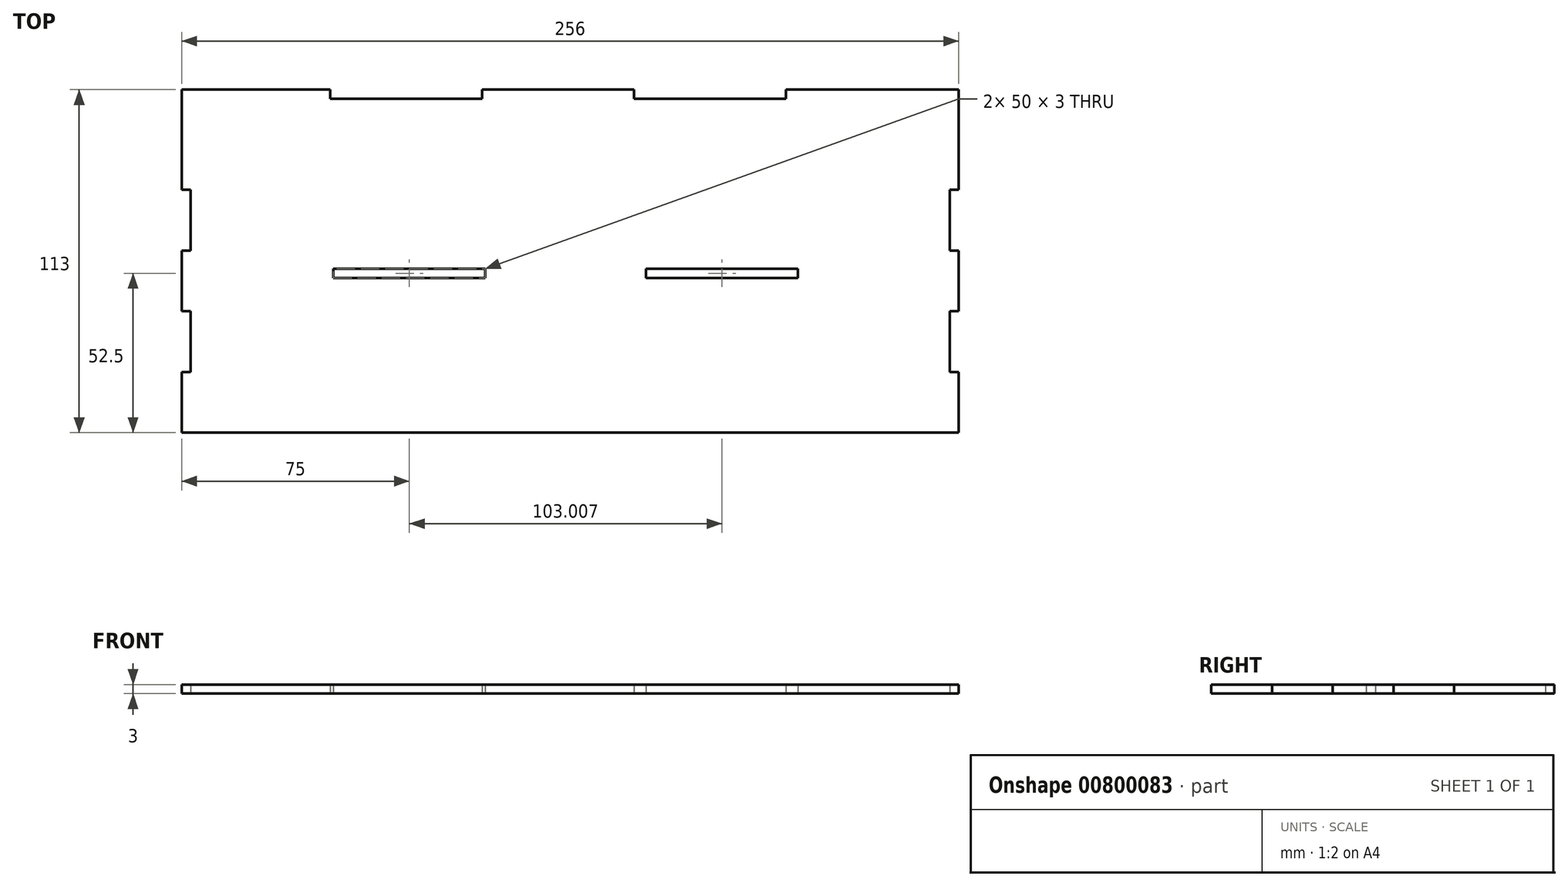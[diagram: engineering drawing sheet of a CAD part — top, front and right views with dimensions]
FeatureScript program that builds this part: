
annotation { "Feature Type Name" : "Feature", "Feature Type Description" : "" }
export const myFeature = defineFeature(function(context is Context, id is Id, definition is map)
    precondition{}
    {
        {
            var Q0;
            Q0=qCreatedBy(makeId("Top.planeOp"),FACE);
            var sketch = newSketch(context, id + "F0", { "sketchPlane" : qUnion([Q0])});
            skLineSegment(sketch, "E0.bottom", {"start": v(-250, 0) * mm, "end": v(0, 0) * mm});
            skLineSegment(sketch, "E0.top", {"start": v(-250, -110) * mm, "end": v(0, -110) * mm});
            skLineSegment(sketch, "E0.left", {"start": v(-250, 0) * mm, "end": v(-250, -110) * mm});
            skLineSegment(sketch, "E0.right", {"start": v(0, 0) * mm, "end": v(0, -110) * mm});
            skLineSegment(sketch, "E1.bottom", {"start": v(-204, 0) * mm, "end": v(-250, 0) * mm});
            skLineSegment(sketch, "E1.top", {"start": v(-204, 3) * mm, "end": v(-250, 3) * mm});
            skLineSegment(sketch, "E1.left", {"start": v(-204, 0) * mm, "end": v(-204, 3) * mm});
            skLineSegment(sketch, "E1.right", {"start": v(-250, 0) * mm, "end": v(-250, 3) * mm});
            skLineSegment(sketch, "E2", {"start": v(-204, 0) * mm, "end": v(-154, 0) * mm});
            skLineSegment(sketch, "E3.bottom", {"start": v(-154, 0) * mm, "end": v(-104, 0) * mm});
            skLineSegment(sketch, "E3.top", {"start": v(-154, 3) * mm, "end": v(-104, 3) * mm});
            skLineSegment(sketch, "E3.left", {"start": v(-154, 0) * mm, "end": v(-154, 3) * mm});
            skLineSegment(sketch, "E3.right", {"start": v(-104, 0) * mm, "end": v(-104, 3) * mm});
            skLineSegment(sketch, "E4", {"start": v(-104, 0) * mm, "end": v(-54, 0) * mm});
            skLineSegment(sketch, "E5.bottom", {"start": v(-54, 0) * mm, "end": v(0, 0) * mm});
            skLineSegment(sketch, "E5.top", {"start": v(-54, 3) * mm, "end": v(0, 3) * mm});
            skLineSegment(sketch, "E5.left", {"start": v(-54, 0) * mm, "end": v(-54, 3) * mm});
            skLineSegment(sketch, "E5.right", {"start": v(0, 0) * mm, "end": v(0, 3) * mm});
            skLineSegment(sketch, "E6.bottom", {"start": v(-250, -110) * mm, "end": v(-253, -110) * mm});
            skLineSegment(sketch, "E6.top", {"start": v(-250, -90) * mm, "end": v(-253, -90) * mm});
            skLineSegment(sketch, "E6.left", {"start": v(-250, -110) * mm, "end": v(-250, -90) * mm});
            skLineSegment(sketch, "E6.right", {"start": v(-253, -110) * mm, "end": v(-253, -90) * mm});
            skLineSegment(sketch, "E7", {"start": v(-250, -90) * mm, "end": v(-250, -70) * mm});
            skLineSegment(sketch, "E8.bottom", {"start": v(-250, -70) * mm, "end": v(-253, -70) * mm});
            skLineSegment(sketch, "E8.top", {"start": v(-250, -50) * mm, "end": v(-253, -50) * mm});
            skLineSegment(sketch, "E8.left", {"start": v(-250, -70) * mm, "end": v(-250, -50) * mm});
            skLineSegment(sketch, "E8.right", {"start": v(-253, -70) * mm, "end": v(-253, -50) * mm});
            skLineSegment(sketch, "E9", {"start": v(-250, -50) * mm, "end": v(-250, -30) * mm});
            skLineSegment(sketch, "E10.bottom", {"start": v(-250, -30) * mm, "end": v(-253, -30) * mm});
            skLineSegment(sketch, "E10.top", {"start": v(-250, 3) * mm, "end": v(-253, 3) * mm});
            skLineSegment(sketch, "E10.left", {"start": v(-250, -30) * mm, "end": v(-250, 3) * mm});
            skLineSegment(sketch, "E10.right", {"start": v(-253, -30) * mm, "end": v(-253, 3) * mm});
            skLineSegment(sketch, "E11.bottom", {"start": v(0, -110) * mm, "end": v(3, -110) * mm});
            skLineSegment(sketch, "E11.top", {"start": v(0, -90) * mm, "end": v(3, -90) * mm});
            skLineSegment(sketch, "E11.left", {"start": v(0, -110) * mm, "end": v(0, -90) * mm});
            skLineSegment(sketch, "E11.right", {"start": v(3, -110) * mm, "end": v(3, -90) * mm});
            skLineSegment(sketch, "E12", {"start": v(0, -90) * mm, "end": v(0, -70) * mm});
            skLineSegment(sketch, "E13.bottom", {"start": v(0, -70) * mm, "end": v(3, -70) * mm});
            skLineSegment(sketch, "E13.top", {"start": v(0, -50) * mm, "end": v(3, -50) * mm});
            skLineSegment(sketch, "E13.left", {"start": v(0, -70) * mm, "end": v(0, -50) * mm});
            skLineSegment(sketch, "E13.right", {"start": v(3, -70) * mm, "end": v(3, -50) * mm});
            skLineSegment(sketch, "E14", {"start": v(0, -50) * mm, "end": v(0, -30) * mm});
            skLineSegment(sketch, "E15.bottom", {"start": v(0, -30) * mm, "end": v(3, -30) * mm});
            skLineSegment(sketch, "E15.top", {"start": v(0, 3) * mm, "end": v(3, 3) * mm});
            skLineSegment(sketch, "E15.left", {"start": v(0, -30) * mm, "end": v(0, 3) * mm});
            skLineSegment(sketch, "E15.right", {"start": v(3, -30) * mm, "end": v(3, 3) * mm});
            skLineSegment(sketch, "E16.bottom", {"start": v(-203, -56) * mm, "end": v(-153, -56) * mm});
            skLineSegment(sketch, "E16.top", {"start": v(-203, -59) * mm, "end": v(-153, -59) * mm});
            skLineSegment(sketch, "E16.left", {"start": v(-203, -56) * mm, "end": v(-203, -59) * mm});
            skLineSegment(sketch, "E16.right", {"start": v(-153, -56) * mm, "end": v(-153, -59) * mm});
            skLineSegment(sketch, "E17.bottom", {"start": v(-100, -56) * mm, "end": v(-50, -56) * mm});
            skLineSegment(sketch, "E17.top", {"start": v(-100, -59) * mm, "end": v(-50, -59) * mm});
            skLineSegment(sketch, "E17.left", {"start": v(-100, -56) * mm, "end": v(-100, -59) * mm});
            skLineSegment(sketch, "E17.right", {"start": v(-50, -56) * mm, "end": v(-50, -59) * mm});
            skSolve(sketch);
        }
        {
            var Q0;
            Q0=qSketchRegion(id+"F0",true);
            extrude(context, id + "F1", {"entities" : qUnion([Q0]), "depth" : 3 * mm, "offsetDistance" : 25.4 * mm});
        }
    });
